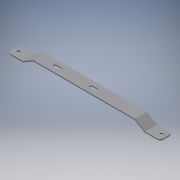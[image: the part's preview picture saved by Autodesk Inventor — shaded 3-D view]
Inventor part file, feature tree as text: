
AUTODESK INVENTOR PART (.ipt)
format: ipt  version: 2016 (Build 200138000, 138)  size: 181,248 bytes
history: native  units: mm
features: sheet_metal_op x7, reference x6, sketch x4, other x4, hole x1, chamfer x1
ambient origin geometry x8: Origin, YZ Plane, XZ Plane, XY Plane, X Axis, Y Axis, Z Axis, Center Point
bodies: Solid1 (feature_tree)
feature tree (23):
  sheet_metal_op  "Face1"
  sheet_metal_op  "Flange1"
  sheet_metal_op  "Flange2"
  hole  "Hole1"  [1 undecoded]
  chamfer  "Corner Round1"
  sketch  "Sketch1"  dims[d0=25.0mm d1=209.0mm]
  other  "Plate1"
  sketch  "Sketch2"  dims[d2=2.0mm]
  other  "Plate2"
  sheet_metal_op  "Bend1"
  sheet_metal_op  "Corner1"
  sketch  "Sketch3"  dims[d3=2.0mm]
  other  "Plate3"
  sheet_metal_op  "Bend2"
  sheet_metal_op  "Corner2"
  sketch  "Sketch4"  dims[d4=1.0mm d5=4.0mm d6=2.0mm d7=25.0mm d8=30.0deg d9=2.0mm d10=8.0mm d11=2.0mm d12=2.0mm d13=2.0mm d14=1.0mm d15=4.0mm d16=2.0mm d17=29.0mm d18=30.0deg d19=2.0mm d20=8.0mm d21=2.0mm d22=2.0mm d23=3.2mm d24=3.2mm d25=10.0mm d26=10.0mm d27=2.0mm d28=0.0mm d31=7.0mm d32=6.0mm d33=4.0mm d34=2.0mm d35=90.0deg d36=2.0mm d37=20.594885mm d38=6.0mm]
  reference  "Reference3"
  reference  "Reference4"
  reference  "Reference5"
  reference  "Reference6"
  reference  "Reference7"
  reference  "Reference8"
  other  "Cut1"
note: 1 required parameter value undecoded (feature->parameter linkage not recoverable at this tier; creation-order binding heuristic only, values carry confidence <= 0.55)
